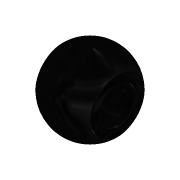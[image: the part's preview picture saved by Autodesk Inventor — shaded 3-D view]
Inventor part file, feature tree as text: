
AUTODESK INVENTOR PART (.ipt)
format: ipt  version: 2021 (Build 250183000, 183)  size: 153,600 bytes
history: native  units: mm (DEFAULTED — no unit token found)
features: other x7, revolve x1, sketch x1
ambient origin geometry x8: Origin, YZ Plane, XZ Plane, XY Plane, X Axis, Y Axis, Z Axis, Center Point
bodies: Solid1 (feature_tree)
feature tree (9):
  revolve  "Revolution1"  [1 undecoded]
  other  "ball_XY"
  other  "ball_YZ"
  other  "ball_ZX"
  other  "ball_X"
  other  "ball_Y"
  other  "ball_Z"
  other  "ball_Center"
  sketch  "Sketch_1"  dims[d0=360.0deg]
note: 1 required parameter value undecoded (feature->parameter linkage not recoverable at this tier; creation-order binding heuristic only, values carry confidence <= 0.55)
